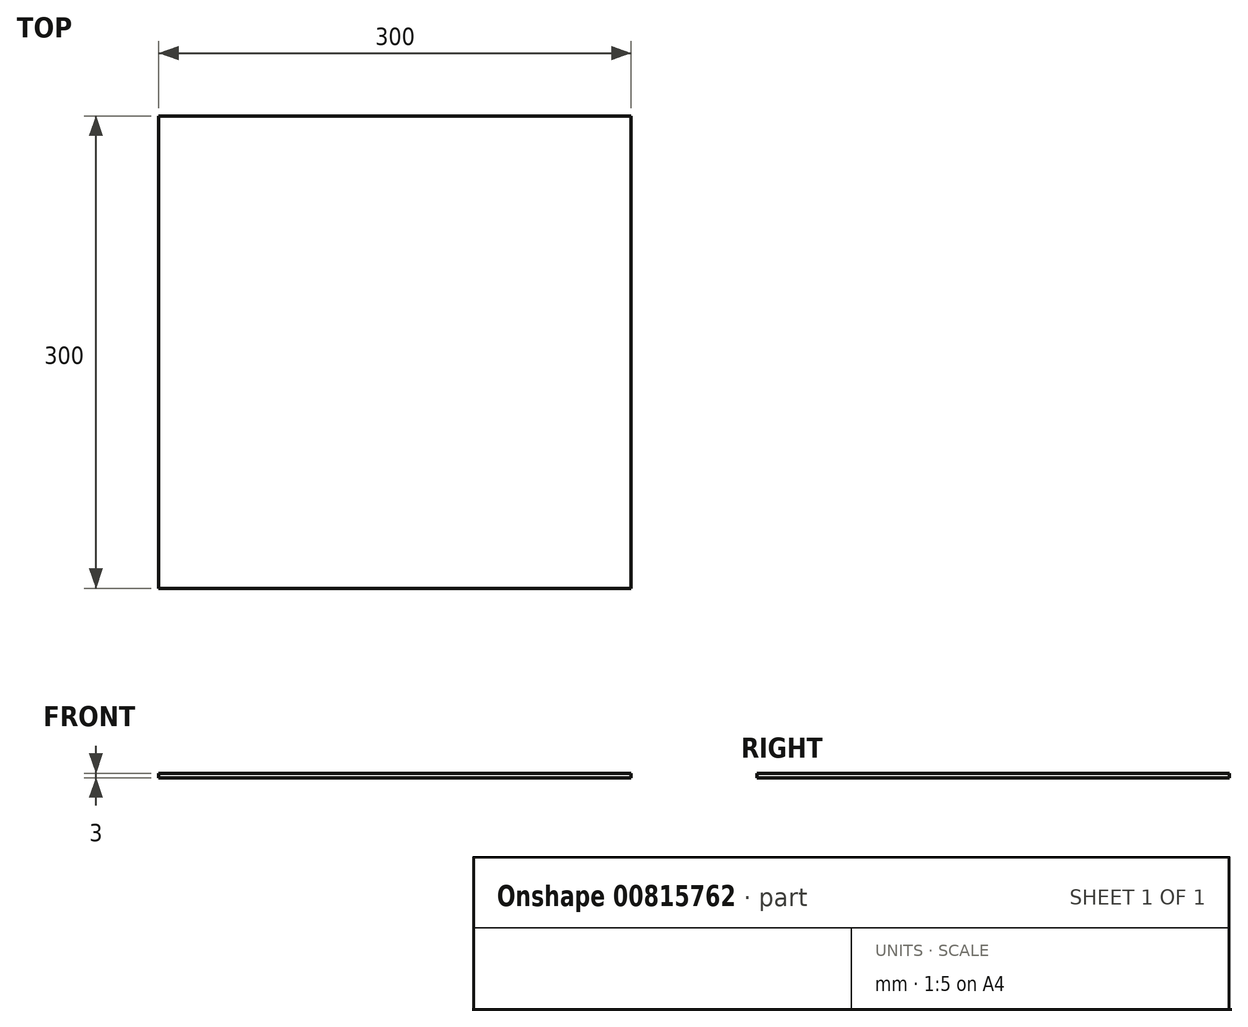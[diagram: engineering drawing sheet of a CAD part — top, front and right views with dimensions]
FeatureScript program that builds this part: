
annotation { "Feature Type Name" : "Feature", "Feature Type Description" : "" }
export const myFeature = defineFeature(function(context is Context, id is Id, definition is map)
    precondition{}
    {
        {
            var Q0;
            Q0=qCreatedBy(makeId("Top.planeOp"),FACE);
            var sketch = newSketch(context, id + "F0", { "sketchPlane" : qUnion([Q0])});
            skLineSegment(sketch, "E0.bottom", {"start": v(150, -150) * mm, "end": v(-150, -150) * mm});
            skLineSegment(sketch, "E0.top", {"start": v(150, 150) * mm, "end": v(-150, 150) * mm});
            skLineSegment(sketch, "E0.left", {"start": v(150, -150) * mm, "end": v(150, 150) * mm});
            skLineSegment(sketch, "E0.right", {"start": v(-150, -150) * mm, "end": v(-150, 150) * mm});
            skPoint(sketch, "E0.middle", {"position": v(0, 0) * mm});
            skSolve(sketch);
        }
        {
            var Q0;
            Q0=makeQuery(id+"F0.imprint","IMPRINT",FACE,{"disambiguationData":[TD([[makeQuery(id+"F0.imprint","IMPRINT",EDGE,{"derivedFrom":sQuery(id+"F0.wireOp",EDGE,"E0.bottom")}),-1.0]])]});
            extrude(context, id + "F1", {"entities" : qUnion([Q0]), "depth" : 3 * mm, "offsetDistance" : 25 * mm});
        }
    });
